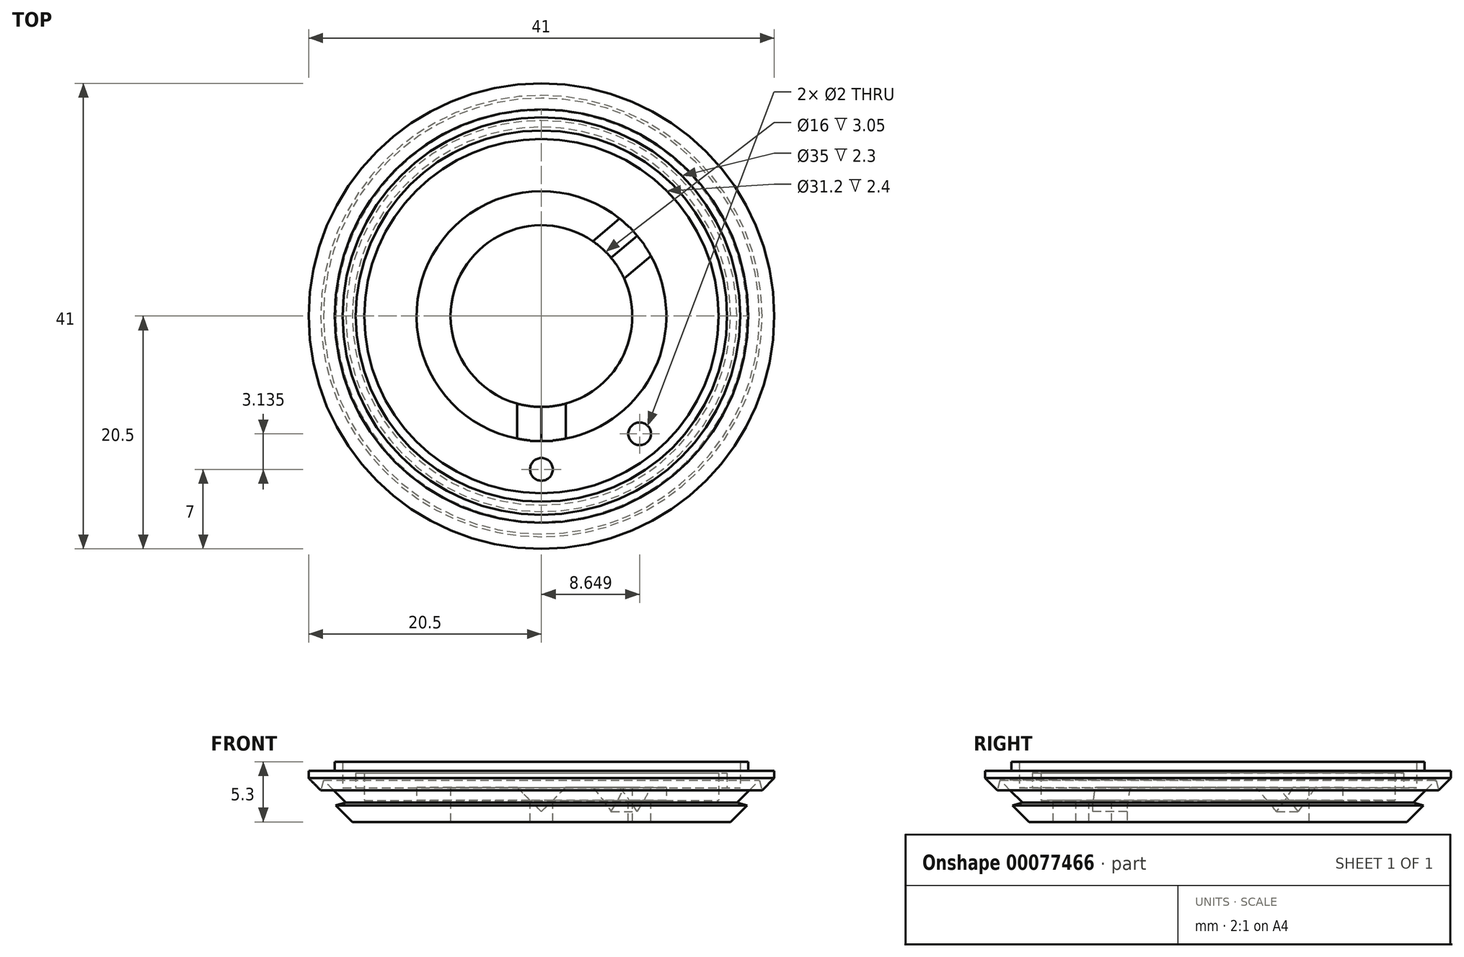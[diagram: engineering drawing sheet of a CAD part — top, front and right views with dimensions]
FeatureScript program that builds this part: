
annotation { "Feature Type Name" : "Feature", "Feature Type Description" : "" }
export const myFeature = defineFeature(function(context is Context, id is Id, definition is map)
    precondition{}
    {
        {
            var Q0;
            Q0=qCreatedBy(makeId("Front.planeOp"),FACE);
            var sketch = newSketch(context, id + "F0", { "sketchPlane" : qUnion([Q0])});
            skLineSegment(sketch, "E0", {"start": v(8, 0) * mm, "end": v(8, 3.05) * mm});
            skLineSegment(sketch, "E1", {"start": v(8, 3.05) * mm, "end": v(11, 3.05) * mm});
            skLineSegment(sketch, "E2", {"start": v(11, 3.05) * mm, "end": v(11, 1.9) * mm});
            skLineSegment(sketch, "E3", {"start": v(11, 1.9) * mm, "end": v(15.6, 1.9) * mm});
            skLineSegment(sketch, "E4", {"start": v(15.6, 1.9) * mm, "end": v(15.6, 4.3) * mm});
            skLineSegment(sketch, "E5", {"start": v(15.6, 4.3) * mm, "end": v(16.35, 4.3) * mm});
            skLineSegment(sketch, "E6", {"start": v(16.35, 4.3) * mm, "end": v(16.35, 3) * mm});
            skLineSegment(sketch, "E7", {"start": v(16.35, 3) * mm, "end": v(17.5, 3) * mm});
            skLineSegment(sketch, "E8", {"start": v(17.5, 3) * mm, "end": v(17.5, 5.3) * mm});
            skLineSegment(sketch, "E9", {"start": v(17.5, 5.3) * mm, "end": v(18.2, 5.3) * mm});
            skLineSegment(sketch, "E10", {"start": v(18.2, 5.3) * mm, "end": v(18.2, 4.5) * mm});
            skLineSegment(sketch, "E11", {"start": v(18.2, 4.5) * mm, "end": v(20.5, 4.5) * mm});
            skLineSegment(sketch, "E12", {"start": v(20.5, 4.5) * mm, "end": v(20.5, 3.85) * mm});
            skLineSegment(sketch, "E13", {"start": v(20.5, 3.85) * mm, "end": v(19.43, 2.78) * mm});
            skLineSegment(sketch, "E14", {"start": v(19.43, 2.78) * mm, "end": v(19.2, 3.68) * mm});
            skLineSegment(sketch, "E15", {"start": v(19.2, 3.68) * mm, "end": v(17.22, 1.7) * mm});
            skLineSegment(sketch, "E16", {"start": v(17.22, 1.7) * mm, "end": v(18.1, 1.46) * mm});
            skLineSegment(sketch, "E17", {"start": v(18.1, 1.46) * mm, "end": v(16.65, 0) * mm});
            skLineSegment(sketch, "E18", {"start": v(16.65, 0) * mm, "end": v(8, 0) * mm});
            skLineSegment(sketch, "E19", {"start": v(19.43, 2.78) * mm, "end": v(18.1, 1.46) * mm, "construction": true});
            skPoint(sketch, "E20", {"position": v(18.77, 2.12) * mm});
            skPoint(sketch, "E21", {"position": v(18.2, 2.69) * mm});
            skLineSegment(sketch, "E22", {"start": v(18.2, 2.69) * mm, "end": v(18.77, 2.12) * mm, "construction": true});
            skLineSegment(sketch, "E23", {"start": v(0, 0) * mm, "end": v(0, 5.3) * mm, "construction": true});
            skSolve(sketch);
        }
        {
            var Q0;
            Q0=makeQuery(id+"F0.imprint","IMPRINT",FACE,{"disambiguationData":[TD([[makeQuery(id+"F0.imprint","IMPRINT",EDGE,{"derivedFrom":sQuery(id+"F0.wireOp",EDGE,"E0")}),-1.0]])]});
            var Q1;
            Q1=sQuery(id+"F0.wireOp",EDGE,"E23");
            revolve(context, id + "F1", {"entities" : qUnion([Q0]), "axis" : qUnion([Q1]), "revolveType" : RevolveType.FULL});
        }
        {
            var Q0;
            Q0=qCreatedBy(makeId("Front.planeOp"),FACE);
            var sketch = newSketch(context, id + "F2", { "sketchPlane" : qUnion([Q0])});
            skLineSegment(sketch, "E24", {"start": v(0, 0) * mm, "end": v(0, 3.05) * mm, "construction": true});
            skLineSegment(sketch, "E25", {"start": v(0, 0.9) * mm, "end": v(2.15, 3.05) * mm});
            skLineSegment(sketch, "E26", {"start": v(0, 0.9) * mm, "end": v(-2.15, 3.05) * mm});
            skLineSegment(sketch, "E27", {"start": v(-2.15, 3.05) * mm, "end": v(2.15, 3.05) * mm});
            skSolve(sketch);
        }
        {
            var Q0;
            Q0=makeQuery(id+"F1.opRevolve","SWEPT_FACE",FACE,{"disambiguationData":[OSD([sQuery(id+"F0.wireOp",EDGE,"E1")])]});
            var sketch = newSketch(context, id + "F3", { "sketchPlane" : qUnion([Q0])});
            skLineSegment(sketch, "E28", {"start": v(0, -11) * mm, "end": v(0, 0) * mm});
            skLineSegment(sketch, "E29", {"start": v(0, 0) * mm, "end": v(8.43, 7.07) * mm});
            skSolve(sketch);
        }
        {
            var Q0;
            Q0=makeQuery(id+"F2.imprint","IMPRINT",FACE,{"disambiguationData":[TD([[makeQuery(id+"F2.imprint","IMPRINT",EDGE,{"derivedFrom":sQuery(id+"F2.wireOp",EDGE,"E25")}),1.0]])]});
            var Q1;
            Q1=sQuery(id+"F3.wireOp",EDGE,"E28");
            sweep(context, id + "F4", {"profiles" : qUnion([Q0]), "path" : qUnion([Q1])});
        }
        {
            var Q0;
            Q0=makeQuery(id+"F4.opSweep","SWEPT_BODY",BODY,{"disambiguationData":[OSD([sQuery(id+"F2.wireOp",EDGE,"E25"),sQuery(id+"F2.wireOp",EDGE,"E26"),sQuery(id+"F2.wireOp",EDGE,"E27"),sQuery(id+"F3.wireOp",EDGE,"E28")])]});
            var Q1;
            Q1=sQuery(id+"F0.wireOp",EDGE,"E23");
            circularPattern(context, id + "F5", {"entities" : qUnion([Q0]), "axis" : qUnion([Q1]), "angle" : 130 * degree, "instanceCount" : 2});
        }
        {
            var Q0;
            Q0=makeQuery(id+"F4.opSweep","SWEPT_BODY",BODY,{"disambiguationData":[OSD([sQuery(id+"F2.wireOp",EDGE,"E25"),sQuery(id+"F2.wireOp",EDGE,"E26"),sQuery(id+"F2.wireOp",EDGE,"E27"),sQuery(id+"F3.wireOp",EDGE,"E28")])]});
            var Q1;
            Q1=makeQuery(id+"F5.opPattern","COPY",BODY,{"derivedFrom":makeQuery(id+"F4.opSweep","SWEPT_BODY",BODY,{"disambiguationData":[OSD([sQuery(id+"F2.wireOp",EDGE,"E25"),sQuery(id+"F2.wireOp",EDGE,"E26"),sQuery(id+"F2.wireOp",EDGE,"E27"),sQuery(id+"F3.wireOp",EDGE,"E28")])]}),"instanceName":"1"});
            var Q2;
            Q2=makeQuery(id+"F1.opRevolve","SWEPT_BODY",BODY,{"disambiguationData":[OSD([sQuery(id+"F0.wireOp",EDGE,"E0"),sQuery(id+"F0.wireOp",EDGE,"E1"),sQuery(id+"F0.wireOp",EDGE,"E2"),sQuery(id+"F0.wireOp",EDGE,"E3"),sQuery(id+"F0.wireOp",EDGE,"E4"),sQuery(id+"F0.wireOp",EDGE,"E5"),sQuery(id+"F0.wireOp",EDGE,"E6"),sQuery(id+"F0.wireOp",EDGE,"E7"),sQuery(id+"F0.wireOp",EDGE,"E8"),sQuery(id+"F0.wireOp",EDGE,"E9"),sQuery(id+"F0.wireOp",EDGE,"E10"),sQuery(id+"F0.wireOp",EDGE,"E11"),sQuery(id+"F0.wireOp",EDGE,"E12"),sQuery(id+"F0.wireOp",EDGE,"E13"),sQuery(id+"F0.wireOp",EDGE,"E14"),sQuery(id+"F0.wireOp",EDGE,"E15"),sQuery(id+"F0.wireOp",EDGE,"E16"),sQuery(id+"F0.wireOp",EDGE,"E17"),sQuery(id+"F0.wireOp",EDGE,"E18")])]});
            booleanBodies(context, id + "F6", {"operationType" : BooleanOperationType.SUBTRACTION, "tools" : qUnion([Q0, Q1]), "targets" : qUnion([Q2])});
        }
        {
            var Q0;
            Q0=makeQuery(id+"F1.opRevolve","SWEPT_FACE",FACE,{"disambiguationData":[OSD([sQuery(id+"F0.wireOp",EDGE,"E3")])]});
            var sketch = newSketch(context, id + "F7", { "sketchPlane" : qUnion([Q0])});
            skCircle(sketch, "E30", {"center": v(0, 0) * mm, "radius": 13.5 * mm, "construction": true});
            skCircle(sketch, "E31", {"center": v(0, -13.5) * mm, "radius": 9.2 * mm, "construction": true});
            skCircle(sketch, "E32", {"center": v(0, -13.5) * mm, "radius": 1 * mm});
            skCircle(sketch, "E33", {"center": v(8.65, -10.37) * mm, "radius": 1 * mm});
            skSolve(sketch);
        }
        {
            var Q0;
            {Q0=qUnion([makeQuery(id+"F7.imprint","IMPRINT",FACE,{"disambiguationData":[TD([[makeQuery(id+"F7.imprint","IMPRINT",EDGE,{"derivedFrom":sQuery(id+"F7.wireOp",EDGE,"E32")}),1.0]])]}),makeQuery(id+"F7.imprint","IMPRINT",FACE,{"disambiguationData":[TD([[makeQuery(id+"F7.imprint","IMPRINT",EDGE,{"derivedFrom":sQuery(id+"F7.wireOp",EDGE,"E33")}),1.0]])]})]);}
            extrude(context, id + "F8", {"entities" : qUnion([Q0]), "operationType" : NewBodyOperationType.REMOVE, "endBound" : BoundingType.THROUGH_ALL, "oppositeDirection" : true, "depth" : 25 * mm});
        }
    });
